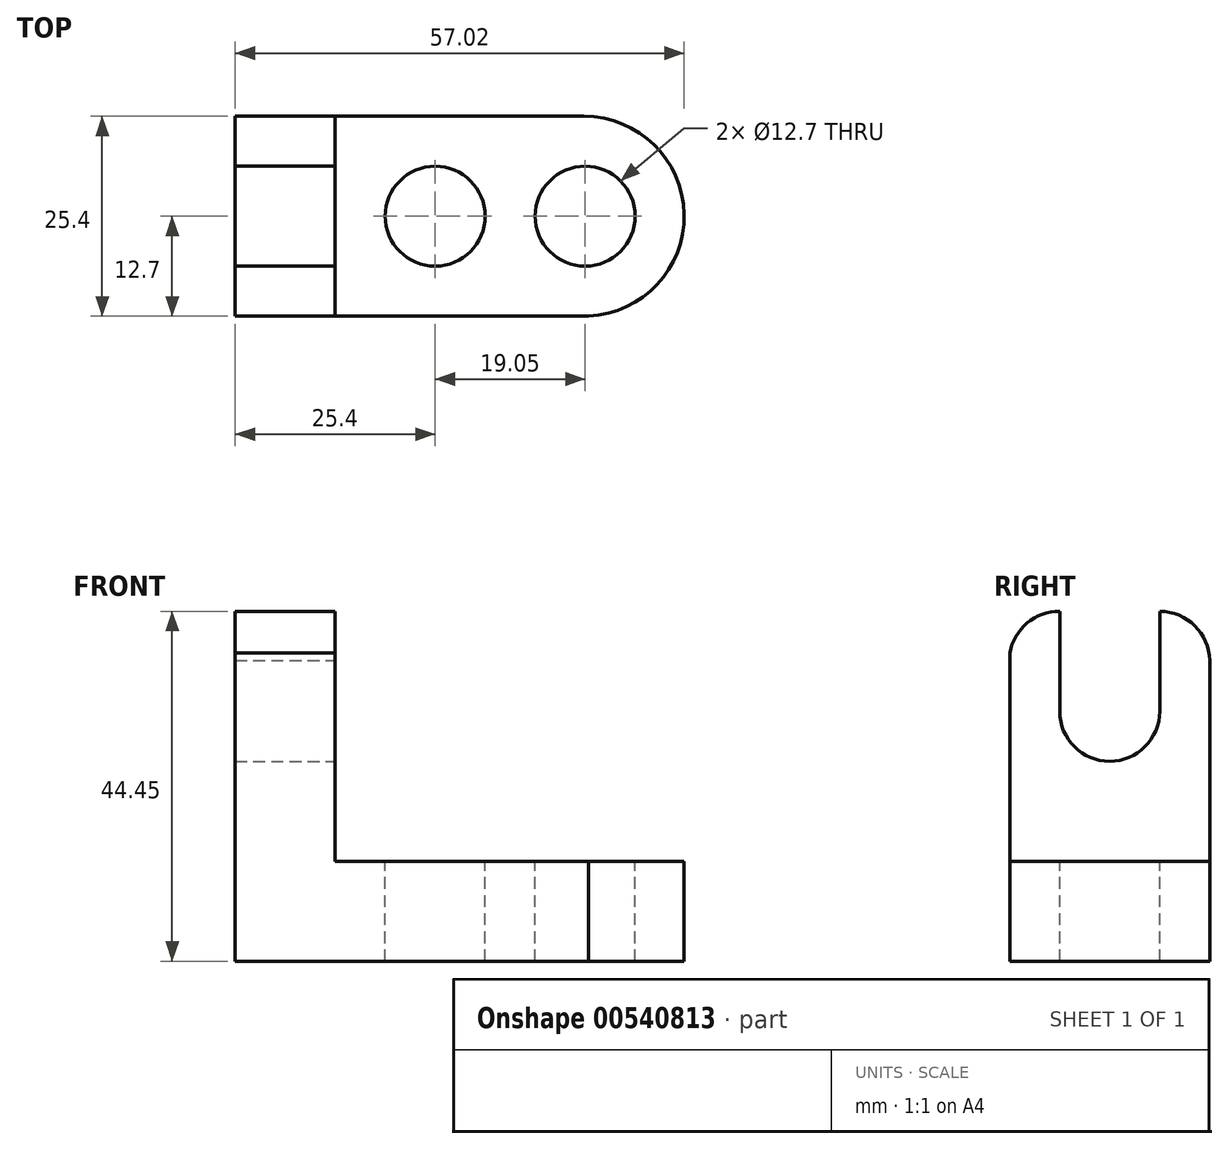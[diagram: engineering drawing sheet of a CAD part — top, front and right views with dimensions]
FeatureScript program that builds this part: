
annotation { "Feature Type Name" : "Feature", "Feature Type Description" : "" }
export const myFeature = defineFeature(function(context is Context, id is Id, definition is map)
    precondition{}
    {
        {
            var Q0;
            Q0=qCreatedBy(makeId("Front.planeOp"),FACE);
            var sketch = newSketch(context, id + "F0", { "sketchPlane" : qUnion([Q0])});
            skLineSegment(sketch, "E0", {"start": v(0, 0) * mm, "end": v(57.15, 0) * mm});
            skLineSegment(sketch, "E1", {"start": v(57.15, 0) * mm, "end": v(57.15, 12.7) * mm});
            skLineSegment(sketch, "E2", {"start": v(57.15, 12.7) * mm, "end": v(12.7, 12.7) * mm});
            skLineSegment(sketch, "E3", {"start": v(12.7, 12.7) * mm, "end": v(12.7, 44.45) * mm});
            skLineSegment(sketch, "E4", {"start": v(12.7, 44.45) * mm, "end": v(0, 44.45) * mm});
            skLineSegment(sketch, "E5", {"start": v(0, 44.45) * mm, "end": v(0, 0) * mm});
            skSolve(sketch);
        }
        {
            var Q0;
            Q0=makeQuery(id+"F0.imprint","IMPRINT",FACE,{"disambiguationData":[TD([[makeQuery(id+"F0.imprint","IMPRINT",EDGE,{"derivedFrom":sQuery(id+"F0.wireOp",EDGE,"E0")}),1.0]])]});
            extrude(context, id + "F1", {"entities" : qUnion([Q0]), "depth" : 25.4 * mm, "offsetDistance" : 25.4 * mm});
        }
        {
            var Q0;
            Q0=makeQuery(id+"F1.opExtrude","SWEPT_FACE",FACE,{"disambiguationData":[OSD([sQuery(id+"F0.wireOp",EDGE,"E3")])]});
            var sketch = newSketch(context, id + "F2", { "sketchPlane" : qUnion([Q0])});
            skLineSegment(sketch, "E6", {"start": v(-19.05, 44.45) * mm, "end": v(-19.05, 31.75) * mm});
            skLineSegment(sketch, "E7", {"start": v(-6.35, 44.45) * mm, "end": v(-19.05, 44.45) * mm});
            skCircle(sketch, "E8", {"center": v(-12.7, 31.75) * mm, "radius": 6.35 * mm});
            skLineSegment(sketch, "E9", {"start": v(-12.7, 44.45) * mm, "end": v(-12.7, 31.75) * mm});
            skLineSegment(sketch, "E10", {"start": v(-6.35, 44.45) * mm, "end": v(-6.35, 31.75) * mm});
            skLineSegment(sketch, "E11", {"start": v(-6.35, 31.75) * mm, "end": v(-19.05, 31.75) * mm});
            skSolve(sketch);
        }
        {
            var Q0;
            {var subQ0=sQuery(id+"F2.wireOp",EDGE,"E6");Q0=makeQuery(id+"F2.imprint","IMPRINT",FACE,{"disambiguationData":[TD([[makeQuery(id+"F2.imprint","IMPRINT",EDGE,{"derivedFrom":subQ0}),1.0]])]});}
            var Q1;
            {var subQ0=sQuery(id+"F2.wireOp",EDGE,"E10");Q1=makeQuery(id+"F2.imprint","IMPRINT",FACE,{"disambiguationData":[TD([[makeQuery(id+"F2.imprint","IMPRINT",EDGE,{"derivedFrom":subQ0}),-1.0]])]});}
            var Q2;
            {var subQ0=sQuery(id+"F2.wireOp",EDGE,"E11");var subQ3=sQuery(id+"F2.wireOp",EDGE,"E9");var subQ5=makeQuery(id+"F2.imprint","INTERSECT",VERTEX,{"derivedFrom":[subQ3,subQ0]});Q2=makeQuery(id+"F2.imprint","IMPRINT",FACE,{"disambiguationData":[TD([[makeQuery(id+"F2.imprint","IMPRINT",EDGE,{"disambiguationData":[TD([[subQ5,1.0]])],"derivedFrom":subQ3}),1.0]])]});}
            var Q3;
            {var subQ0=sQuery(id+"F2.wireOp",EDGE,"E11");var subQ3=sQuery(id+"F2.wireOp",EDGE,"E9");var subQ5=makeQuery(id+"F2.imprint","INTERSECT",VERTEX,{"derivedFrom":[subQ3,subQ0]});Q3=makeQuery(id+"F2.imprint","IMPRINT",FACE,{"disambiguationData":[TD([[makeQuery(id+"F2.imprint","IMPRINT",EDGE,{"disambiguationData":[TD([[subQ5,1.0]])],"derivedFrom":subQ3}),-1.0]])]});}
            var Q4;
            {var subQ0=sQuery(id+"F2.wireOp",EDGE,"E11");var subQ4=makeQuery(id+"F2.imprint","INTERSECT",VERTEX,{"derivedFrom":[sQuery(id+"F2.wireOp",EDGE,"E9"),subQ0]});Q4=makeQuery(id+"F2.imprint","IMPRINT",FACE,{"disambiguationData":[TD([[makeQuery(id+"F2.imprint","IMPRINT",EDGE,{"disambiguationData":[TD([[subQ4,1.0]])],"derivedFrom":subQ0}),1.0]])]});}
            extrude(context, id + "F3", {"entities" : qUnion([Q0, Q1, Q2, Q3, Q4]), "operationType" : NewBodyOperationType.REMOVE, "oppositeDirection" : true, "depth" : 25.4 * mm, "offsetDistance" : 25.4 * mm});
        }
        {
            var Q0;
            Q0=makeQuery(id+"F1.opExtrude","SWEPT_FACE",FACE,{"disambiguationData":[OSD([sQuery(id+"F0.wireOp",EDGE,"E2")])]});
            var sketch = newSketch(context, id + "F4", { "sketchPlane" : qUnion([Q0])});
            skCircle(sketch, "E12", {"center": v(25.4, -12.7) * mm, "radius": 6.35 * mm});
            skCircle(sketch, "E13", {"center": v(44.45, -12.7) * mm, "radius": 6.35 * mm});
            skSolve(sketch);
        }
        {
            var Q0;
            Q0=makeQuery(id+"F4.imprint","IMPRINT",FACE,{"disambiguationData":[TD([[makeQuery(id+"F4.imprint","IMPRINT",EDGE,{"derivedFrom":sQuery(id+"F4.wireOp",EDGE,"E12")}),1.0]])]});
            var Q1;
            Q1=makeQuery(id+"F4.imprint","IMPRINT",FACE,{"disambiguationData":[TD([[makeQuery(id+"F4.imprint","IMPRINT",EDGE,{"derivedFrom":sQuery(id+"F4.wireOp",EDGE,"E13")}),1.0]])]});
            extrude(context, id + "F5", {"entities" : qUnion([Q0, Q1]), "operationType" : NewBodyOperationType.REMOVE, "oppositeDirection" : true, "depth" : 25.4 * mm, "offsetDistance" : 25.4 * mm});
        }
        {
            var Q0;
            Q0=makeQuery(id+"F1.opExtrude","SWEPT_FACE",FACE,{"disambiguationData":[OSD([sQuery(id+"F0.wireOp",EDGE,"E3")])]});
            var sketch = newSketch(context, id + "F6", { "sketchPlane" : qUnion([Q0])});
            skArc(sketch, "E14", {"start": v(-19.05, 44.45) * mm, "mid": v(-23.19, 42.95) * mm, "end": v(-25.4, 39.14) * mm});
            skArc(sketch, "E15", {"start": v(0, 38) * mm, "mid": v(-1.82, 42.55) * mm, "end": v(-6.35, 44.45) * mm});
            skSolve(sketch);
        }
        {
            var Q0;
            {var subQ0=sQuery(id+"F6.wireOp",EDGE,"E14");Q0=makeQuery(id+"F6.imprint","IMPRINT",FACE,{"disambiguationData":[TD([[makeQuery(id+"F6.imprint","IMPRINT",EDGE,{"derivedFrom":subQ0}),-1.0]])]});}
            var Q1;
            {var subQ1=sQuery(id+"F0.wireOp",EDGE,"E4");var subQ2=sQuery(id+"F0.wireOp",EDGE,"E3");var subQ3=sQuery(id+"F2.wireOp",EDGE,"E10");var subQ4=makeQuery(id+"F3.boolean.opBoolean","SPLIT",EDGE,{"disambiguationData":[TD([makeQuery(id+"F3.opExtrude","SWEPT_FACE",FACE,{"disambiguationData":[OSD([subQ3])]})])],"derivedFrom":makeQuery(id+"F1.opExtrude","SWEPT_EDGE",EDGE,{"disambiguationData":[OSD([subQ2,subQ1])]})});Q1=makeQuery(id+"F6.imprint","IMPRINT",FACE,{"disambiguationData":[TD([[makeQuery(id+"F6.imprint","IMPRINT",EDGE,{"derivedFrom":subQ4}),-1.0]])]});}
            extrude(context, id + "F7", {"entities" : qUnion([Q0, Q1]), "operationType" : NewBodyOperationType.REMOVE, "oppositeDirection" : true, "depth" : 25.4 * mm, "offsetDistance" : 25.4 * mm});
        }
        {
            var Q0;
            Q0=makeQuery(id+"F1.opExtrude","SWEPT_FACE",FACE,{"disambiguationData":[OSD([sQuery(id+"F0.wireOp",EDGE,"E2")])]});
            var sketch = newSketch(context, id + "F8", { "sketchPlane" : qUnion([Q0])});
            skArc(sketch, "E16", {"start": v(44.9, -25.4) * mm, "mid": v(57.01, -12.42) * mm, "end": v(44.32, 0) * mm});
            skSolve(sketch);
        }
        {
            var Q0;
            {var subQ0=sQuery(id+"F8.wireOp",EDGE,"E16");Q0=makeQuery(id+"F8.imprint","IMPRINT",FACE,{"disambiguationData":[TD([[makeQuery(id+"F8.imprint","IMPRINT",EDGE,{"derivedFrom":subQ0}),-1.0]])]});}
            extrude(context, id + "F9", {"entities" : qUnion([Q0]), "operationType" : NewBodyOperationType.REMOVE, "oppositeDirection" : true, "depth" : 25.4 * mm, "offsetDistance" : 25.4 * mm});
        }
    });
